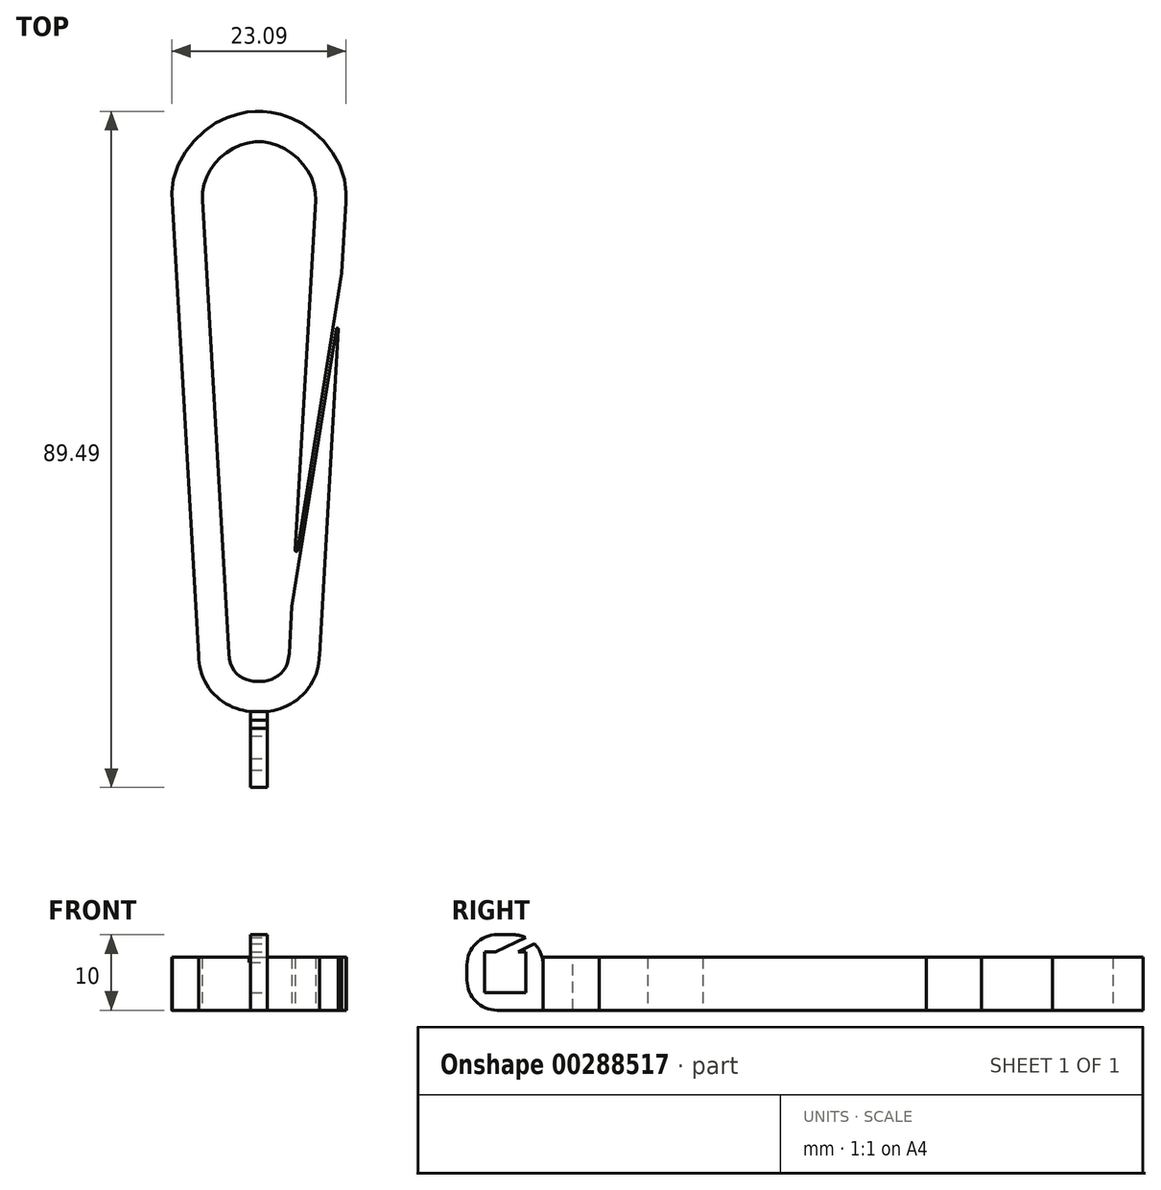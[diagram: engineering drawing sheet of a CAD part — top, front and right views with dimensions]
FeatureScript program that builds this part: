
annotation { "Feature Type Name" : "Feature", "Feature Type Description" : "" }
export const myFeature = defineFeature(function(context is Context, id is Id, definition is map)
    precondition{}
    {
        {
            var Q0;
            Q0=qCreatedBy(makeId("Top.planeOp"),FACE);
            var sketch = newSketch(context, id + "F0", { "sketchPlane" : qUnion([Q0])});
            skLineSegment(sketch, "E0", {"start": v(0, 0) * mm, "end": v(-7.5, 0) * mm, "construction": true});
            skLineSegment(sketch, "E1", {"start": v(0, 0) * mm, "end": v(7.5, 0) * mm, "construction": true});
            skLineSegment(sketch, "E2", {"start": v(0, 0) * mm, "end": v(0, -60) * mm, "construction": true});
            skLineSegment(sketch, "E3", {"start": v(0, -60) * mm, "end": v(-4, -60) * mm, "construction": true});
            skLineSegment(sketch, "E4", {"start": v(0, -60) * mm, "end": v(4, -60) * mm, "construction": true});
            skLineSegment(sketch, "E5", {"start": v(-7.5, 0) * mm, "end": v(-4, -60) * mm});
            skLineSegment(sketch, "E6", {"start": v(4, -60) * mm, "end": v(4.36, -53.8) * mm});
            skFitSpline(sketch, "E7", {"points": [v(-4, -60) * mm, v(0, -63.73) * mm, v(4, -60) * mm], "startDerivative": vector(0.97, -16.68) * mm, "endDerivative": vector(0.94, 16.09) * mm});
            skFitSpline(sketch, "E8", {"points": [v(-7.5, 0) * mm, v(0, 7.75) * mm, v(7.5, 0) * mm], "startDerivative": vector(-1.46, 24.98) * mm, "endDerivative": vector(-1.4, -24.16) * mm});
            skLineSegment(sketch, "E9.0", {"start": v(-11.5, -0.23) * mm, "end": v(-8, -60.23) * mm});
            skFitSpline(sketch, "E9.1", {"points": [v(-11.5, -0.23) * mm, v(-11.54, 0.61) * mm, v(-11.43, 2.28) * mm, v(-10.73, 4.57) * mm, v(-9.61, 6.6) * mm, v(-8.17, 8.33) * mm, v(-6.45, 9.76) * mm, v(-4.82, 10.68) * mm, v(-3.4, 11.22) * mm, v(-2.3, 11.52) * mm, v(-1.35, 11.68) * mm, v(-0.56, 11.74) * mm, v(0.04, 11.76) * mm, v(0.63, 11.73) * mm, v(1.41, 11.66) * mm, v(2.37, 11.48) * mm, v(3.47, 11.16) * mm, v(4.86, 10.6) * mm, v(6.47, 9.67) * mm, v(8.17, 8.24) * mm, v(9.6, 6.52) * mm, v(10.72, 4.52) * mm, v(11.42, 2.26) * mm, v(11.54, 0.6) * mm, v(11.5, -0.23) * mm]});
            skLineSegment(sketch, "E9.2", {"start": v(8, -60.23) * mm, "end": v(10.5, -17.1) * mm});
            skFitSpline(sketch, "E9.3", {"points": [v(-8, -60.23) * mm, v(-7.96, -60.8) * mm, v(-7.8, -61.93) * mm, v(-7.23, -63.53) * mm, v(-6.34, -64.95) * mm, v(-5.17, -66.1) * mm, v(-3.86, -66.92) * mm, v(-2.52, -67.43) * mm, v(-1.43, -67.65) * mm, v(-0.57, -67.72) * mm, v(0.05, -67.73) * mm, v(0.67, -67.7) * mm, v(1.52, -67.6) * mm, v(2.6, -67.37) * mm, v(3.91, -66.85) * mm, v(5.19, -66.03) * mm, v(6.33, -64.9) * mm, v(7.22, -63.5) * mm, v(7.8, -61.92) * mm, v(7.96, -60.8) * mm, v(8, -60.23) * mm]});
            skLineSegment(sketch, "E10", {"start": v(10.94, -9.64) * mm, "end": v(5.07, -46.38) * mm});
            skLineSegment(sketch, "E11", {"start": v(4.36, -53.8) * mm, "end": v(10.23, -17.06) * mm});
            skLineSegment(sketch, "E12.trimOffspring", {"start": v(10.94, -9.64) * mm, "end": v(11.5, -0.23) * mm});
            skLineSegment(sketch, "E13.trimOffspring", {"start": v(4.8, -46.35) * mm, "end": v(7.5, 0) * mm});
            skPoint(sketch, "E14.visualSharp", {"position": v(10.67, -14.3) * mm});
            skArc(sketch, "E14.filletArc", {"start": v(10.5, -17.1) * mm, "mid": v(10.39, -16.95) * mm, "end": v(10.23, -17.06) * mm});
            skPoint(sketch, "E15.visualSharp", {"position": v(4.63, -49.14) * mm});
            skArc(sketch, "E15.filletArc", {"start": v(4.8, -46.35) * mm, "mid": v(4.92, -46.5) * mm, "end": v(5.07, -46.38) * mm});
            skLineSegment(sketch, "E16", {"start": v(-1.12, -77.73) * mm, "end": v(-1.12, -67.67) * mm});
            skLineSegment(sketch, "E17", {"start": v(1.13, -77.73) * mm, "end": v(1.13, -67.65) * mm});
            skPoint(sketch, "E18.start.orphan", {"position": v(0, -67.73) * mm});
            skLineSegment(sketch, "E19", {"start": v(-1.12, -77.73) * mm, "end": v(1.13, -77.73) * mm});
            skSolve(sketch);
        }
        {
            var Q0;
            Q0=makeQuery(id+"F0.imprint","IMPRINT",FACE,{"disambiguationData":[TD([[makeQuery(id+"F0.imprint","IMPRINT",EDGE,{"derivedFrom":sQuery(id+"F0.wireOp",EDGE,"E5")}),-1.0]])]});
            extrude(context, id + "F1", {"entities" : qUnion([Q0]), "depth" : 7 * mm});
        }
        {
            var Q0;
            {var subQ0=sQuery(id+"F0.wireOp",EDGE,"E16");Q0=makeQuery(id+"F0.imprint","IMPRINT",FACE,{"disambiguationData":[TD([[makeQuery(id+"F0.imprint","IMPRINT",EDGE,{"derivedFrom":subQ0}),-1.0]])]});}
            extrude(context, id + "F2", {"entities" : qUnion([Q0]), "operationType" : NewBodyOperationType.ADD, "depth" : 10 * mm});
        }
        {
            var Q0;
            Q0=makeQuery(id+"F2.opExtrude","SWEPT_FACE",FACE,{"disambiguationData":[OSD([sQuery(id+"F0.wireOp",EDGE,"E17")])]});
            var sketch = newSketch(context, id + "F3", { "sketchPlane" : qUnion([Q0])});
            skLineSegment(sketch, "E20", {"start": v(-67.65, 10) * mm, "end": v(-77.73, 0) * mm, "construction": true});
            skLineSegment(sketch, "E21", {"start": v(-67.65, 0) * mm, "end": v(-77.73, 10) * mm, "construction": true});
            skLineSegment(sketch, "E22.1", {"start": v(-75.43, 7.7) * mm, "end": v(-73.92, 7.7) * mm});
            skLineSegment(sketch, "E22.3", {"start": v(-75.43, 2.3) * mm, "end": v(-69.95, 2.3) * mm});
            skLineSegment(sketch, "E22.4", {"start": v(-75.43, 7.7) * mm, "end": v(-75.43, 2.3) * mm});
            skLineSegment(sketch, "E23", {"start": v(-69.95, 7.7) * mm, "end": v(-69.95, 2.3) * mm});
            skLineSegment(sketch, "E24", {"start": v(-73.73, 10) * mm, "end": v(-71.65, 10) * mm});
            skLineSegment(sketch, "E25", {"start": v(-67.65, 0) * mm, "end": v(-67.65, 6) * mm});
            skLineSegment(sketch, "E26", {"start": v(-77.73, 4) * mm, "end": v(-77.73, 6) * mm});
            skLineSegment(sketch, "E27", {"start": v(-73.73, 0) * mm, "end": v(-67.65, 0) * mm});
            skPoint(sketch, "E28.visualSharp", {"position": v(-77.73, 10) * mm});
            skArc(sketch, "E28.filletArc", {"start": v(-73.73, 10) * mm, "mid": v(-76.56, 8.83) * mm, "end": v(-77.73, 6) * mm});
            skPoint(sketch, "E29.visualSharp", {"position": v(-67.65, 10) * mm});
            skArc(sketch, "E29.filletArc", {"start": v(-67.65, 6) * mm, "mid": v(-68.82, 8.83) * mm, "end": v(-71.65, 10) * mm});
            skPoint(sketch, "E30.visualSharp", {"position": v(-77.73, 0) * mm});
            skArc(sketch, "E30.filletArc", {"start": v(-77.73, 4) * mm, "mid": v(-76.56, 1.17) * mm, "end": v(-73.73, 0) * mm});
            skLineSegment(sketch, "E31", {"start": v(-73.92, 7.7) * mm, "end": v(-69.92, 9.6) * mm});
            skLineSegment(sketch, "E32", {"start": v(-70.95, 7.7) * mm, "end": v(-68.83, 8.83) * mm});
            skLineSegment(sketch, "E33.trimOffspring", {"start": v(-70.95, 7.7) * mm, "end": v(-69.95, 7.7) * mm});
            skSolve(sketch);
        }
        {
            var Q0;
            Q0=makeQuery(id+"F3.imprint","IMPRINT",FACE,{"disambiguationData":[TD([[makeQuery(id+"F3.imprint","IMPRINT",EDGE,{"derivedFrom":sQuery(id+"F3.wireOp",EDGE,"E22.1")}),-1.0]])]});
            var Q1;
            {var subQ0=sQuery(id+"F3.wireOp",EDGE,"E28.filletArc");Q1=makeQuery(id+"F3.imprint","IMPRINT",FACE,{"disambiguationData":[TD([[makeQuery(id+"F3.imprint","IMPRINT",EDGE,{"derivedFrom":subQ0}),-1.0]])]});}
            var Q2;
            {var subQ0=sQuery(id+"F3.wireOp",EDGE,"E29.filletArc");Q2=makeQuery(id+"F3.imprint","IMPRINT",FACE,{"disambiguationData":[TD([[makeQuery(id+"F3.imprint","IMPRINT",EDGE,{"derivedFrom":subQ0}),-1.0]])]});}
            var Q3;
            {var subQ0=sQuery(id+"F3.wireOp",EDGE,"E30.filletArc");Q3=makeQuery(id+"F3.imprint","IMPRINT",FACE,{"disambiguationData":[TD([[makeQuery(id+"F3.imprint","IMPRINT",EDGE,{"derivedFrom":subQ0}),-1.0]])]});}
            extrude(context, id + "F4", {"entities" : qUnion([Q0, Q1, Q2, Q3]), "operationType" : NewBodyOperationType.REMOVE, "oppositeDirection" : true, "depth" : 25 * mm});
        }
    });
